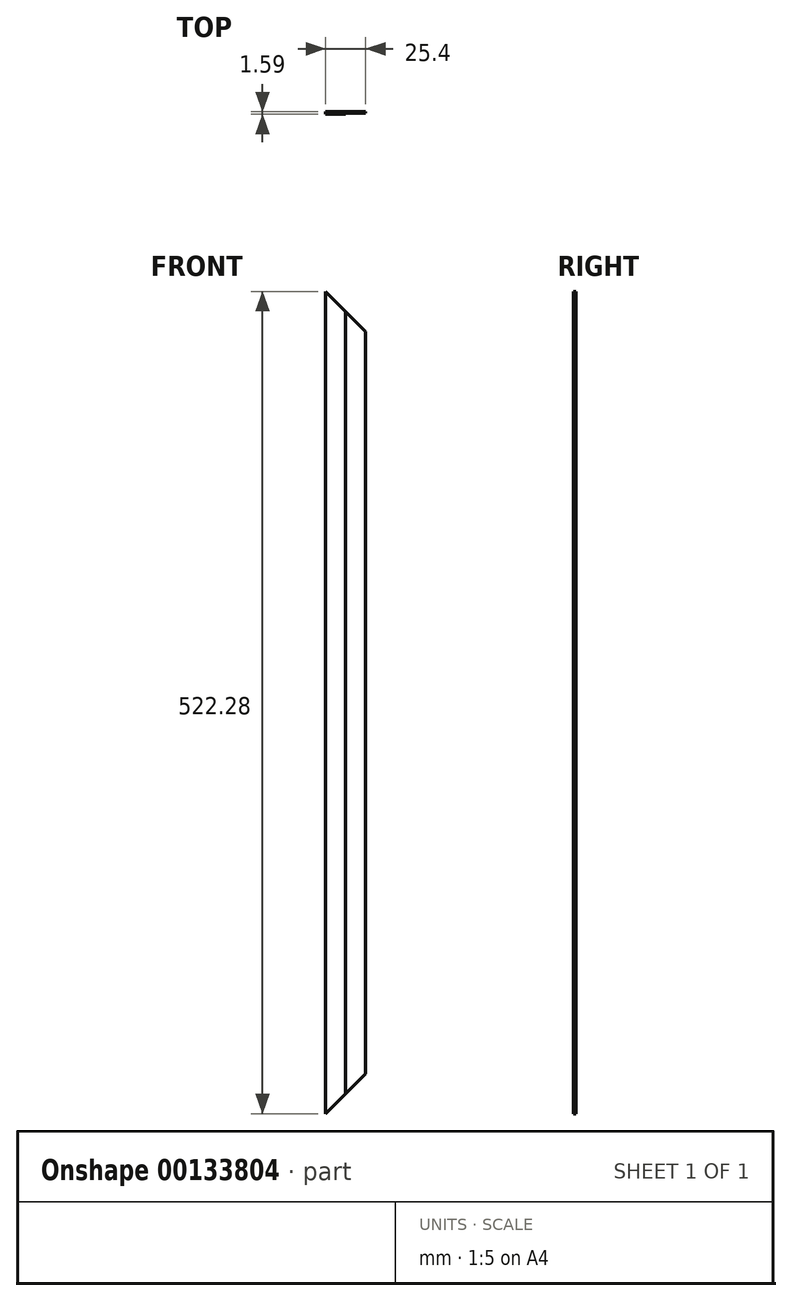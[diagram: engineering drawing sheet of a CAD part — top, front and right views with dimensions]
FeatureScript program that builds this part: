
annotation { "Feature Type Name" : "Feature", "Feature Type Description" : "" }
export const myFeature = defineFeature(function(context is Context, id is Id, definition is map)
    precondition{}
    {
        {
            var Q0;
            Q0=qCreatedBy(makeId("Front.planeOp"),FACE);
            var sketch = newSketch(context, id + "F0", { "sketchPlane" : qUnion([Q0])});
            skLineSegment(sketch, "E0", {"start": v(-25.4, 261.14) * mm, "end": v(-25.4, -261.14) * mm});
            skLineSegment(sketch, "E1", {"start": v(-25.4, -261.14) * mm, "end": v(0, -235.74) * mm});
            skLineSegment(sketch, "E2", {"start": v(0, -235.74) * mm, "end": v(0, 235.74) * mm});
            skLineSegment(sketch, "E3", {"start": v(0, 235.74) * mm, "end": v(-25.4, 261.14) * mm});
            skPoint(sketch, "E4", {"position": v(0, 0) * mm});
            skSolve(sketch);
        }
        {
            var Q0;
            Q0 = qSketchRegion(id + "F0", true);
            extrude(context, id + "F1", {"entities" : qUnion([Q0]), "depth" : 1.59 * mm});
        }
        {
            var Q0;
            Q0=makeQuery(id+"F1.opExtrude","CAP_FACE",FACE,{"disambiguationData":[OSD([sQuery(id+"F0.wireOp",EDGE,"E0"),sQuery(id+"F0.wireOp",EDGE,"E1"),sQuery(id+"F0.wireOp",EDGE,"E2"),sQuery(id+"F0.wireOp",EDGE,"E3")])],"isStart":false});
            var sketch = newSketch(context, id + "F2", { "sketchPlane" : qUnion([Q0])});
            skLineSegment(sketch, "E5", {"start": v(0, -235.74) * mm, "end": v(-12.7, -248.44) * mm});
            skLineSegment(sketch, "E6", {"start": v(-12.7, -248.44) * mm, "end": v(-12.7, 248.44) * mm});
            skLineSegment(sketch, "E7", {"start": v(-12.7, 248.44) * mm, "end": v(0, 235.74) * mm});
            skLineSegment(sketch, "E8", {"start": v(0, 235.74) * mm, "end": v(0, -235.74) * mm});
            skSolve(sketch);
        }
        {
            var Q0;
            Q0 = qSketchRegion(id + "F2", true);
            extrude(context, id + "F3", {"entities" : qUnion([Q0]), "operationType" : NewBodyOperationType.REMOVE, "oppositeDirection" : true, "depth" : 0.8 * mm});
        }
    });
